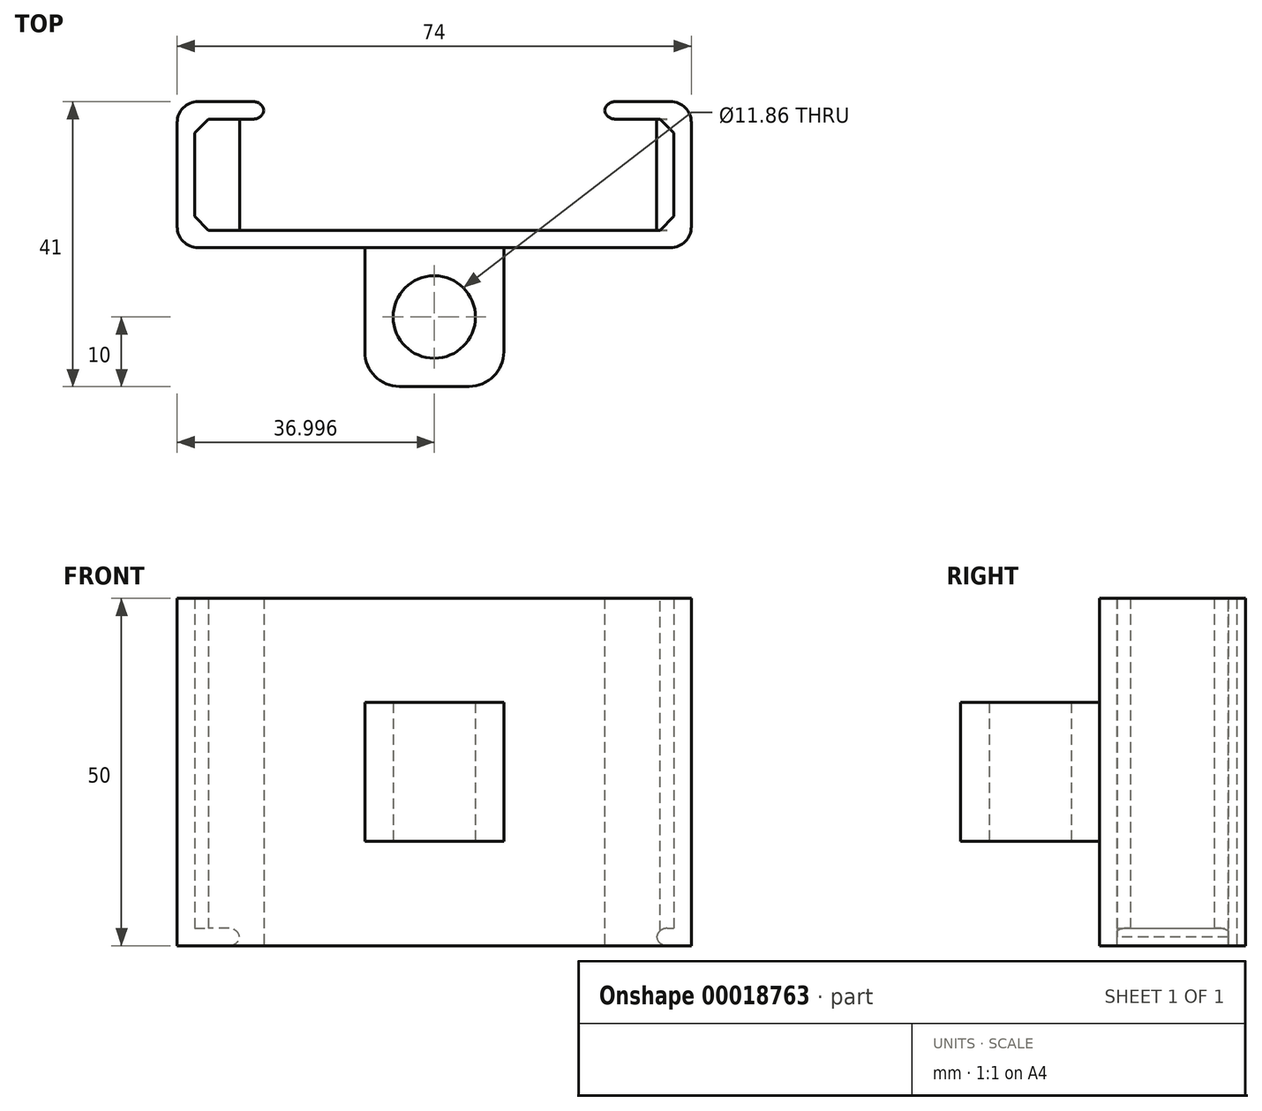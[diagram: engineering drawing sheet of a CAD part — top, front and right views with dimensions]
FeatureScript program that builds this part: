
annotation { "Feature Type Name" : "Feature", "Feature Type Description" : "" }
export const myFeature = defineFeature(function(context is Context, id is Id, definition is map)
    precondition{}
    {
        {
            var Q0;
            Q0=qCreatedBy(makeId("Top.planeOp"),FACE);
            var sketch = newSketch(context, id + "F0", { "sketchPlane" : qUnion([Q0])});
            skLineSegment(sketch, "E0", {"start": v(-24.4, 18.5) * mm, "end": v(-11.9, 18.5) * mm});
            skLineSegment(sketch, "E1", {"start": v(-11.9, 18.5) * mm, "end": v(-11.9, 16) * mm});
            skLineSegment(sketch, "E2", {"start": v(-11.9, 16) * mm, "end": v(-21.9, 16) * mm});
            skLineSegment(sketch, "E3", {"start": v(-21.9, 16) * mm, "end": v(-21.9, 0) * mm});
            skLineSegment(sketch, "E4", {"start": v(-21.9, 0) * mm, "end": v(47.1, 0) * mm});
            skLineSegment(sketch, "E5", {"start": v(47.1, 0) * mm, "end": v(47.1, 16) * mm});
            skLineSegment(sketch, "E6", {"start": v(47.1, 16) * mm, "end": v(37.1, 16) * mm});
            skLineSegment(sketch, "E7", {"start": v(37.1, 16) * mm, "end": v(37.1, 18.5) * mm});
            skLineSegment(sketch, "E8", {"start": v(37.1, 18.5) * mm, "end": v(49.6, 18.5) * mm});
            skLineSegment(sketch, "E9", {"start": v(49.6, 18.5) * mm, "end": v(49.6, -2.5) * mm});
            skLineSegment(sketch, "E10", {"start": v(49.6, -2.5) * mm, "end": v(-24.4, -2.5) * mm});
            skLineSegment(sketch, "E11", {"start": v(-24.4, -2.5) * mm, "end": v(-24.4, 18.5) * mm});
            skLineSegment(sketch, "E12", {"start": v(-15.4, 0) * mm, "end": v(-15.4, 16) * mm});
            skLineSegment(sketch, "E13", {"start": v(44.6, 0) * mm, "end": v(44.6, 16) * mm});
            skSolve(sketch);
        }
        {
            var Q0;
            Q0=makeQuery(id+"F0.imprint","IMPRINT",FACE,{"disambiguationData":[TD([[makeQuery(id+"F0.imprint","IMPRINT",EDGE,{"derivedFrom":sQuery(id+"F0.wireOp",EDGE,"E0")}),-1.0]])]});
            extrude(context, id + "F1", {"entities" : qUnion([Q0]), "depth" : 50 * mm});
        }
        {
            var Q0;
            {var subQ2=sQuery(id+"F0.wireOp",EDGE,"E5");Q0=makeQuery(id+"F0.imprint","IMPRINT",FACE,{"disambiguationData":[TD([[makeQuery(id+"F0.imprint","IMPRINT",EDGE,{"derivedFrom":subQ2}),1.0]])]});}
            var Q1;
            {var subQ2=sQuery(id+"F0.wireOp",EDGE,"E3");Q1=makeQuery(id+"F0.imprint","IMPRINT",FACE,{"disambiguationData":[TD([[makeQuery(id+"F0.imprint","IMPRINT",EDGE,{"derivedFrom":subQ2}),1.0]])]});}
            extrude(context, id + "F2", {"entities" : qUnion([Q0, Q1]), "operationType" : NewBodyOperationType.ADD, "depth" : 2.5 * mm});
        }
        {
            var Q0;
            Q0=makeQuery(id+"F1.opExtrude","SWEPT_EDGE",EDGE,{"disambiguationData":[OSD([sQuery(id+"F0.wireOp",EDGE,"E4"),sQuery(id+"F0.wireOp",EDGE,"E5")])]});
            var Q1;
            Q1=makeQuery(id+"F1.opExtrude","SWEPT_EDGE",EDGE,{"disambiguationData":[OSD([sQuery(id+"F0.wireOp",EDGE,"E5"),sQuery(id+"F0.wireOp",EDGE,"E6")])]});
            var Q2;
            Q2=makeQuery(id+"F1.opExtrude","SWEPT_EDGE",EDGE,{"disambiguationData":[OSD([sQuery(id+"F0.wireOp",EDGE,"E3"),sQuery(id+"F0.wireOp",EDGE,"E4")])]});
            var Q3;
            Q3=makeQuery(id+"F1.opExtrude","SWEPT_EDGE",EDGE,{"disambiguationData":[OSD([sQuery(id+"F0.wireOp",EDGE,"E2"),sQuery(id+"F0.wireOp",EDGE,"E3")])]});
            chamfer(context, id + "F3", {"entities" : qUnion([Q0, Q1, Q2, Q3]), "width" : 2 * mm, "tangentPropagation" : true});
        }
        {
            var Q0;
            Q0=makeQuery(id+"F1.opExtrude","SWEPT_EDGE",EDGE,{"disambiguationData":[OSD([sQuery(id+"F0.wireOp",EDGE,"E0"),sQuery(id+"F0.wireOp",EDGE,"E11")])]});
            var Q1;
            Q1=makeQuery(id+"F1.opExtrude","SWEPT_EDGE",EDGE,{"disambiguationData":[OSD([sQuery(id+"F0.wireOp",EDGE,"E10"),sQuery(id+"F0.wireOp",EDGE,"E11")])]});
            var Q2;
            Q2=makeQuery(id+"F1.opExtrude","SWEPT_EDGE",EDGE,{"disambiguationData":[OSD([sQuery(id+"F0.wireOp",EDGE,"E9"),sQuery(id+"F0.wireOp",EDGE,"E10")])]});
            var Q3;
            Q3=makeQuery(id+"F1.opExtrude","SWEPT_EDGE",EDGE,{"disambiguationData":[OSD([sQuery(id+"F0.wireOp",EDGE,"E8"),sQuery(id+"F0.wireOp",EDGE,"E9")])]});
            fillet(context, id + "F4", {"entities" : qUnion([Q0, Q1, Q2, Q3]), "radius" : 3 * mm, "tangentPropagation" : true, "allowEdgeOverflow" : false});
        }
        {
            var Q0;
            Q0=makeQuery(id+"F1.opExtrude","SWEPT_EDGE",EDGE,{"disambiguationData":[OSD([sQuery(id+"F0.wireOp",EDGE,"E1"),sQuery(id+"F0.wireOp",EDGE,"E2")])]});
            var Q1;
            Q1=makeQuery(id+"F1.opExtrude","SWEPT_EDGE",EDGE,{"disambiguationData":[OSD([sQuery(id+"F0.wireOp",EDGE,"E0"),sQuery(id+"F0.wireOp",EDGE,"E1")])]});
            var Q2;
            Q2=makeQuery(id+"F1.opExtrude","SWEPT_EDGE",EDGE,{"disambiguationData":[OSD([sQuery(id+"F0.wireOp",EDGE,"E7"),sQuery(id+"F0.wireOp",EDGE,"E8")])]});
            var Q3;
            Q3=makeQuery(id+"F1.opExtrude","SWEPT_EDGE",EDGE,{"disambiguationData":[OSD([sQuery(id+"F0.wireOp",EDGE,"E6"),sQuery(id+"F0.wireOp",EDGE,"E7")])]});
            var Q4;
            Q4=makeQuery(id+"F2.opExtrude","CAP_EDGE",EDGE,{"disambiguationData":[OSD([sQuery(id+"F0.wireOp",EDGE,"E13")])],"isStart":false});
            var Q5;
            Q5=makeQuery(id+"F2.opExtrude","CAP_EDGE",EDGE,{"disambiguationData":[OSD([sQuery(id+"F0.wireOp",EDGE,"E13")])],"isStart":true});
            var Q6;
            Q6=makeQuery(id+"F2.opExtrude","CAP_EDGE",EDGE,{"disambiguationData":[OSD([sQuery(id+"F0.wireOp",EDGE,"E12")])],"isStart":false});
            var Q7;
            Q7=makeQuery(id+"F2.opExtrude","CAP_EDGE",EDGE,{"disambiguationData":[OSD([sQuery(id+"F0.wireOp",EDGE,"E12")])],"isStart":true});
            fillet(context, id + "F5", {"entities" : qUnion([Q0, Q1, Q2, Q3, Q4, Q5, Q6, Q7]), "radius" : 1.5 * mm, "tangentPropagation" : true, "allowEdgeOverflow" : false});
        }
        {
            var Q0;
            Q0=makeQuery(id+"F1.opExtrude","SWEPT_FACE",FACE,{"disambiguationData":[OSD([sQuery(id+"F0.wireOp",EDGE,"E10")])]});
            var sketch = newSketch(context, id + "F6", { "sketchPlane" : qUnion([Q0])});
            skLineSegment(sketch, "E14.bottom", {"start": v(22.6, 35) * mm, "end": v(2.6, 35) * mm});
            skLineSegment(sketch, "E14.top", {"start": v(22.6, 15) * mm, "end": v(2.6, 15) * mm});
            skLineSegment(sketch, "E14.left", {"start": v(22.6, 35) * mm, "end": v(22.6, 15) * mm});
            skLineSegment(sketch, "E14.right", {"start": v(2.6, 35) * mm, "end": v(2.6, 15) * mm});
            skSolve(sketch);
        }
        {
            var Q0;
            Q0 = qSketchRegion(id + "F6", true);
            extrude(context, id + "F7", {"entities" : qUnion([Q0]), "operationType" : NewBodyOperationType.ADD, "depth" : 20 * mm});
        }
        {
            var Q0;
            Q0=makeQuery(id+"F7.opExtrude","SWEPT_FACE",FACE,{"disambiguationData":[OSD([sQuery(id+"F6.wireOp",EDGE,"E14.top")])]});
            var sketch = newSketch(context, id + "F8", { "sketchPlane" : qUnion([Q0])});
            skCircle(sketch, "E15", {"center": v(12.6, 12.5) * mm, "radius": 5.93 * mm});
            skSolve(sketch);
        }
        {
            var Q0;
            Q0 = qSketchRegion(id + "F8", true);
            extrude(context, id + "F9", {"entities" : qUnion([Q0]), "operationType" : NewBodyOperationType.REMOVE, "oppositeDirection" : true, "depth" : 25 * mm});
        }
        {
            var Q0;
            Q0=makeQuery(id+"F7.opExtrude","CAP_EDGE",EDGE,{"disambiguationData":[OSD([sQuery(id+"F6.wireOp",EDGE,"E14.right")])],"isStart":true});
            var Q1;
            Q1=makeQuery(id+"F7.opExtrude","CAP_EDGE",EDGE,{"disambiguationData":[OSD([sQuery(id+"F6.wireOp",EDGE,"E14.right")])],"isStart":false});
            var Q2;
            Q2=makeQuery(id+"F7.opExtrude","CAP_EDGE",EDGE,{"disambiguationData":[OSD([sQuery(id+"F6.wireOp",EDGE,"E14.left")])],"isStart":false});
            var Q3;
            Q3=makeQuery(id+"F7.opExtrude","CAP_EDGE",EDGE,{"disambiguationData":[OSD([sQuery(id+"F6.wireOp",EDGE,"E14.left")])],"isStart":true});
            var Q4;
            Q4=makeQuery(id+"F7.opExtrude","CAP_EDGE",EDGE,{"disambiguationData":[OSD([sQuery(id+"F6.wireOp",EDGE,"E14.top")])],"isStart":true});
            var Q5;
            Q5=makeQuery(id+"F7.opExtrude","CAP_EDGE",EDGE,{"disambiguationData":[OSD([sQuery(id+"F6.wireOp",EDGE,"E14.bottom")])],"isStart":true});
            fillet(context, id + "F10", {"entities" : qUnion([Q0, Q1, Q2, Q3, Q4, Q5]), "radius" : 5 * mm, "tangentPropagation" : true, "allowEdgeOverflow" : false});
        }
    });
